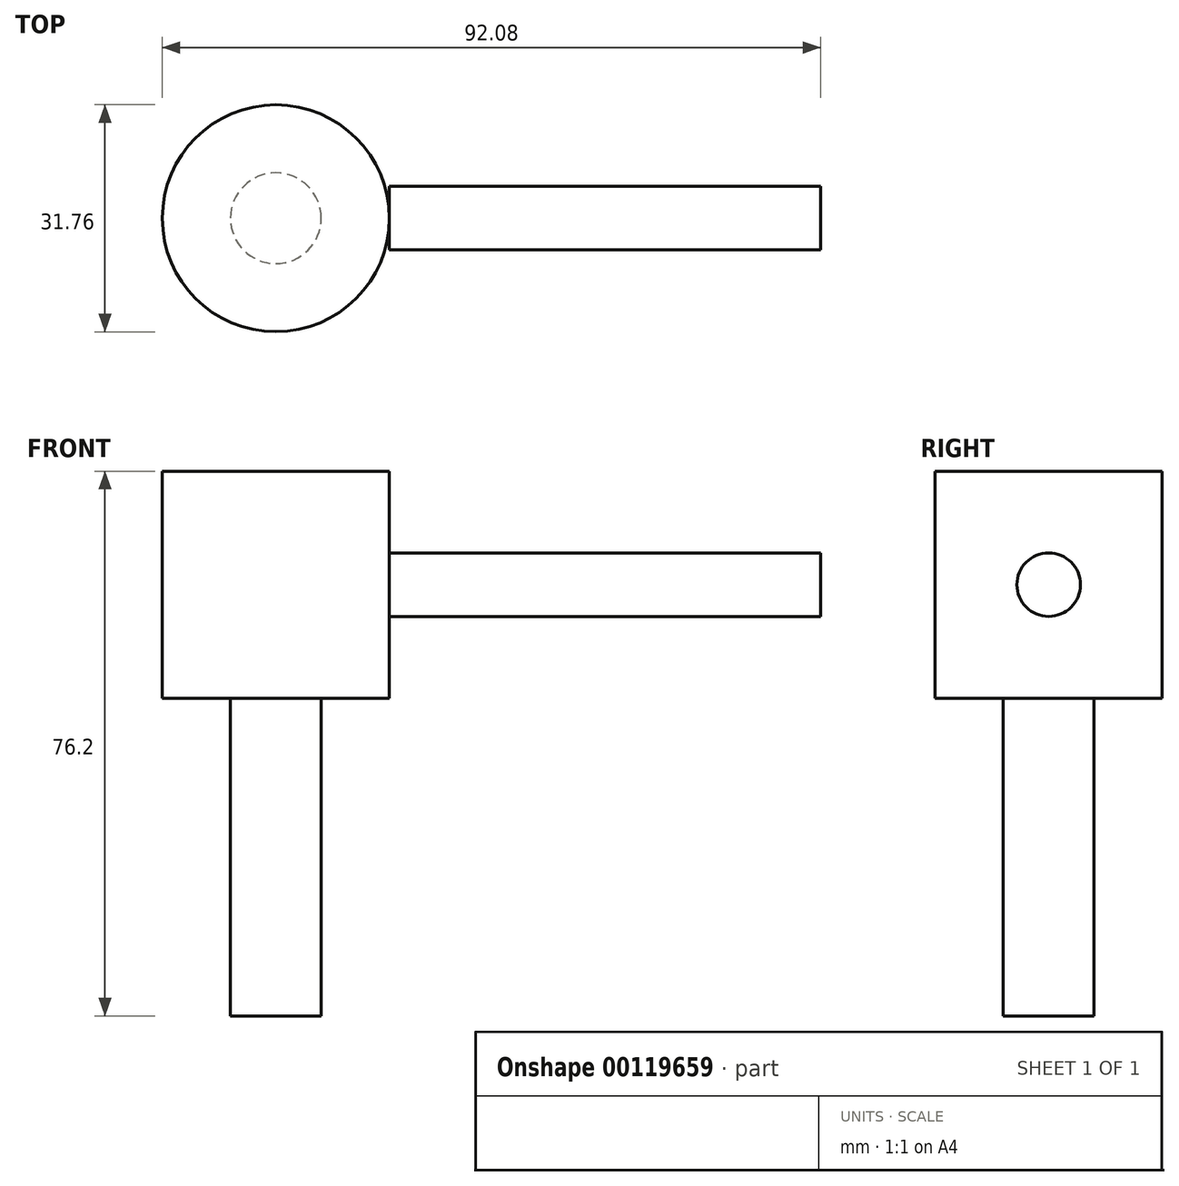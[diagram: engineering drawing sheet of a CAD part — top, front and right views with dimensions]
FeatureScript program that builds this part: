
annotation { "Feature Type Name" : "Feature", "Feature Type Description" : "" }
export const myFeature = defineFeature(function(context is Context, id is Id, definition is map)
    precondition{}
    {
        {
            var Q0;
            Q0=qCreatedBy(makeId("Front.planeOp"),FACE);
            var sketch = newSketch(context, id + "F0", { "sketchPlane" : qUnion([Q0])});
            skLineSegment(sketch, "E0", {"start": v(0, 0) * mm, "end": v(0, 31.75) * mm});
            skLineSegment(sketch, "E1", {"start": v(0, 31.75) * mm, "end": v(15.88, 31.75) * mm});
            skLineSegment(sketch, "E2", {"start": v(15.88, 31.75) * mm, "end": v(15.88, 0) * mm});
            skLineSegment(sketch, "E3", {"start": v(15.88, 0) * mm, "end": v(0, 0) * mm});
            skLineSegment(sketch, "E4", {"start": v(15.88, 15.88) * mm, "end": v(76.2, 15.88) * mm});
            skLineSegment(sketch, "E5", {"start": v(76.2, 15.88) * mm, "end": v(76.2, 20.32) * mm});
            skLineSegment(sketch, "E6", {"start": v(76.2, 20.32) * mm, "end": v(15.88, 20.32) * mm});
            skPoint(sketch, "E7", {"position": v(15.88, 15.88) * mm});
            skLineSegment(sketch, "E8.MirrorCS", {"start": v(-76.2, 20.32) * mm, "end": v(-15.88, 20.32) * mm});
            skLineSegment(sketch, "E9.MirrorCS", {"start": v(-15.88, 15.88) * mm, "end": v(-76.2, 15.88) * mm});
            skLineSegment(sketch, "E10.MirrorCS", {"start": v(-76.2, 15.88) * mm, "end": v(-76.2, 20.32) * mm});
            skLineSegment(sketch, "E11.MirrorCS", {"start": v(-15.88, 31.75) * mm, "end": v(-15.88, 0) * mm});
            skLineSegment(sketch, "E12.MirrorCS", {"start": v(0, 31.75) * mm, "end": v(-15.88, 31.75) * mm});
            skLineSegment(sketch, "E13.MirrorCS", {"start": v(-15.88, 0) * mm, "end": v(0, 0) * mm});
            skLineSegment(sketch, "E14", {"start": v(76.2, 15.88) * mm, "end": v(76.2, 11.43) * mm});
            skLineSegment(sketch, "E15", {"start": v(76.2, 11.43) * mm, "end": v(15.88, 11.43) * mm, "construction": true});
            skArc(sketch, "E16", {"start": v(76.2, 11.43) * mm, "mid": v(95.5, 15.87) * mm, "end": v(76.2, 20.32) * mm});
            skSolve(sketch);
        }
        {
            var Q0;
            Q0=makeQuery(id+"F0.imprint","IMPRINT",FACE,{"disambiguationData":[TD([[makeQuery(id+"F0.imprint","IMPRINT",EDGE,{"derivedFrom":sQuery(id+"F0.wireOp",EDGE,"E0")}),-1.0]])]});
            var Q1;
            Q1=sQuery(id+"F0.wireOp",EDGE,"E0");
            revolve(context, id + "F1", {"entities" : qUnion([Q0]), "axis" : qUnion([Q1]), "revolveType" : RevolveType.FULL});
        }
        {
            var Q0;
            {var subQ0=sQuery(id+"F0.wireOp",EDGE,"E4");Q0=makeQuery(id+"F0.imprint","IMPRINT",FACE,{"disambiguationData":[TD([[makeQuery(id+"F0.imprint","IMPRINT",EDGE,{"derivedFrom":subQ0}),1.0]])]});}
            var Q1;
            Q1=sQuery(id+"F0.wireOp",EDGE,"E4");
            revolve(context, id + "F2", {"entities" : qUnion([Q0]), "axis" : qUnion([Q1]), "revolveType" : RevolveType.FULL});
        }
        {
            var Q0;
            Q0=makeQuery(id+"F1.opRevolve","SWEPT_FACE",FACE,{"disambiguationData":[OSD([sQuery(id+"F0.wireOp",EDGE,"E3")])]});
            var sketch = newSketch(context, id + "F3", { "sketchPlane" : qUnion([Q0])});
            skCircle(sketch, "E17", {"center": v(0, 0) * mm, "radius": 6.35 * mm});
            skSolve(sketch);
        }
        {
            var Q0;
            Q0=makeQuery(id+"F3.imprint","IMPRINT",FACE,{"disambiguationData":[TD([[makeQuery(id+"F3.imprint","IMPRINT",EDGE,{"derivedFrom":sQuery(id+"F3.wireOp",EDGE,"E17")}),1.0]])]});
            var Q1;
            Q1=sQuery(id+"F3.wireOp",EDGE,"E17");
            extrude(context, id + "F4", {"entities" : qUnion([Q0]), "operationType" : NewBodyOperationType.ADD, "surfaceEntities" : qUnion([Q1]), "depth" : 44.45 * mm});
        }
    });
